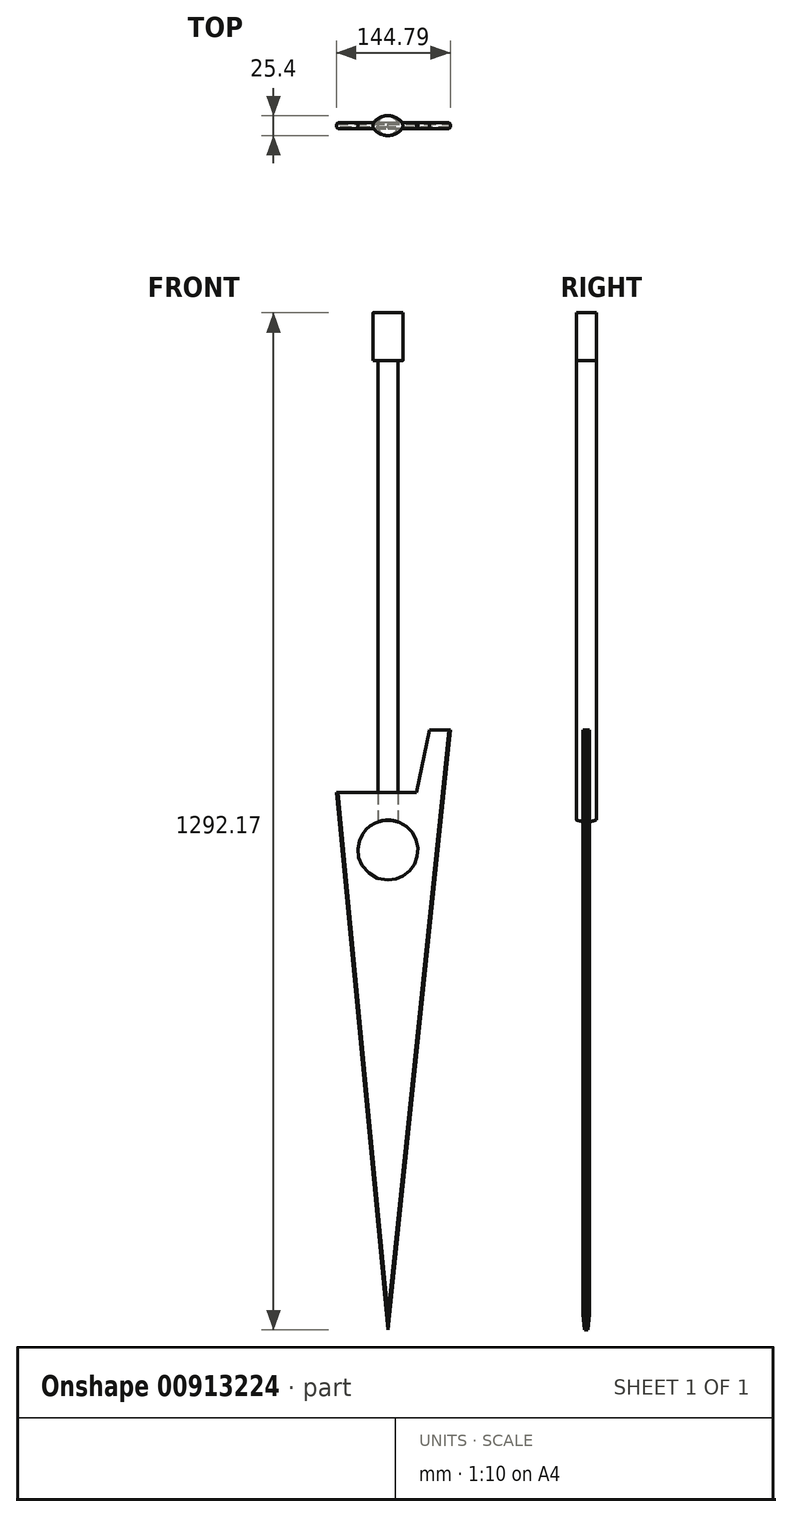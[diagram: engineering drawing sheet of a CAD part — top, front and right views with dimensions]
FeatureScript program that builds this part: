
annotation { "Feature Type Name" : "Feature", "Feature Type Description" : "" }
export const myFeature = defineFeature(function(context is Context, id is Id, definition is map)
    precondition{}
    {
        {
            var Q0;
            Q0=qCreatedBy(makeId("Front.planeOp"),FACE);
            var sketch = newSketch(context, id + "F0", { "sketchPlane" : qUnion([Q0])});
            skLineSegment(sketch, "E0", {"start": v(0, 0) * mm, "end": v(0, 609.6) * mm, "construction": true});
            skLineSegment(sketch, "E1", {"start": v(0, 0) * mm, "end": v(0, -609.6) * mm, "construction": true});
            skLineSegment(sketch, "E2", {"start": v(28.58, 0) * mm, "end": v(28.58, 304.8) * mm, "construction": true});
            skLineSegment(sketch, "E3", {"start": v(79.37, 152.4) * mm, "end": v(0, -609.6) * mm});
            skLineSegment(sketch, "E4", {"start": v(28.58, 152.4) * mm, "end": v(-73.03, 152.4) * mm, "construction": true});
            skLineSegment(sketch, "E5", {"start": v(-65.41, 72.97) * mm, "end": v(0, -609.6) * mm});
            skCircle(sketch, "E6", {"center": v(0, 0) * mm, "radius": 38.1 * mm});
            skPoint(sketch, "E7.orphan", {"position": v(-38.1, 0) * mm});
            skLineSegment(sketch, "E8", {"start": v(28.58, 152.4) * mm, "end": v(23.49, 72.97) * mm});
            skLineSegment(sketch, "E9", {"start": v(23.49, 72.97) * mm, "end": v(-65.41, 72.97) * mm});
            skLineSegment(sketch, "E10", {"start": v(28.58, 152.4) * mm, "end": v(79.38, 152.4) * mm});
            skPoint(sketch, "E11.orphan", {"position": v(95.36, 305.86) * mm});
            skLineSegment(sketch, "E12", {"start": v(-38.1, 0) * mm, "end": v(-58.42, 0) * mm, "construction": true});
            skLineSegment(sketch, "E13", {"start": v(38.1, 0) * mm, "end": v(63.5, 0) * mm, "construction": true});
            skSolve(sketch);
        }
        {
            var Q0;
            Q0=makeQuery(id+"F0.imprint","IMPRINT",FACE,{"disambiguationData":[TD([[makeQuery(id+"F0.imprint","IMPRINT",EDGE,{"derivedFrom":sQuery(id+"F0.wireOp",EDGE,"E3")}),-1.0]])]});
            extrude(context, id + "F1", {"entities" : qUnion([Q0]), "endBound" : BoundingType.SYMMETRIC, "depth" : 7.94 * mm, "offsetDistance" : 30.48 * mm});
        }
        {
            var Q0;
            Q0=makeQuery(id+"F1.opExtrude","SWEPT_FACE",FACE,{"disambiguationData":[OSD([sQuery(id+"F0.wireOp",EDGE,"E9")])]});
            var sketch = newSketch(context, id + "F2", { "sketchPlane" : qUnion([Q0])});
            skCircle(sketch, "E14", {"center": v(0, 0) * mm, "radius": 12.7 * mm});
            skSolve(sketch);
        }
        {
            var Q0;
            Q0 = qSketchRegion(id + "F2", true);
            var Q1;
            Q1=makeQuery(id+"F1.opExtrude","SWEPT_FACE",FACE,{"disambiguationData":[OSD([sQuery(id+"F0.wireOp",EDGE,"E6")])]});
            extrude(context, id + "F3", {"entities" : qUnion([Q0]), "depth" : 609.6 * mm, "offsetDistance" : 30.48 * mm, "hasSecondDirection" : true, "secondDirectionBound" : SecondDirectionBoundingType.UP_TO_SURFACE, "secondDirectionOppositeDirection" : true, "secondDirectionDepth" : 25.4 * mm, "secondDirectionBoundEntityFace" : qUnion([Q1])});
        }
        {
            var Q0;
            {var subQ0=sQuery(id+"F2.wireOp",EDGE,"E14");var subQ1=sQuery(id+"F0.wireOp",EDGE,"E9");var subQ2=makeQuery(id+"F1.opExtrude","CAP_EDGE",EDGE,{"disambiguationData":[OSD([subQ1])],"isStart":true});var subQ3=makeQuery(id+"F2.imprint","INTERSECT",VERTEX,{"disambiguationData":[OD(0.0)],"derivedFrom":[subQ2,subQ0]});Q0=makeQuery(id+"F3.opExtrude","CAP_FACE",FACE,{"disambiguationData":[OSD([subQ0]),topologyDisambiguationEdgeConnected([makeQuery(id+"F2.imprint","IMPRINT",EDGE,{"disambiguationData":[TD([[subQ3,1.0]])],"derivedFrom":subQ0})])],"isStart":false});}
            var sketch = newSketch(context, id + "F4", { "sketchPlane" : qUnion([Q0])});
            skLineSegment(sketch, "E15.bottom", {"start": v(22.86, 12.7) * mm, "end": v(-22.86, 12.7) * mm});
            skLineSegment(sketch, "E15.top", {"start": v(22.86, -12.7) * mm, "end": v(-22.86, -12.7) * mm});
            skLineSegment(sketch, "E15.left", {"start": v(22.86, 12.7) * mm, "end": v(22.86, -12.7) * mm});
            skLineSegment(sketch, "E15.right", {"start": v(-22.86, 12.7) * mm, "end": v(-22.86, -12.7) * mm});
            skPoint(sketch, "E15.middle", {"position": v(0, 0) * mm});
            skSolve(sketch);
        }
        {
            var Q0;
            Q0 = qSketchRegion(id + "F4", true);
            extrude(context, id + "F5", {"entities" : qUnion([Q0]), "operationType" : NewBodyOperationType.ADD, "oppositeDirection" : true, "depth" : 60.96 * mm, "offsetDistance" : 30.48 * mm});
        }
        {
            var Q0;
            Q0=makeQuery(id+"F5.opExtrude","SWEPT_EDGE",EDGE,{"disambiguationData":[OSD([sQuery(id+"F4.wireOp",EDGE,"E15.top"),sQuery(id+"F4.wireOp",EDGE,"E15.left")])]});
            var Q1;
            Q1=makeQuery(id+"F5.opExtrude","SWEPT_EDGE",EDGE,{"disambiguationData":[OSD([sQuery(id+"F4.wireOp",EDGE,"E15.top"),sQuery(id+"F4.wireOp",EDGE,"E15.right")])]});
            var Q2;
            Q2=makeQuery(id+"F5.opExtrude","SWEPT_EDGE",EDGE,{"disambiguationData":[OSD([sQuery(id+"F4.wireOp",EDGE,"E15.bottom"),sQuery(id+"F4.wireOp",EDGE,"E15.right")])]});
            var Q3;
            Q3=makeQuery(id+"F5.opExtrude","SWEPT_EDGE",EDGE,{"disambiguationData":[OSD([sQuery(id+"F4.wireOp",EDGE,"E15.bottom"),sQuery(id+"F4.wireOp",EDGE,"E15.left")])]});
            fillet(context, id + "F6", {"entities" : qUnion([Q0, Q1, Q2, Q3]), "radius" : 22.86 * mm, "tangentPropagation" : true, "allowEdgeOverflow" : false});
        }
        {
            var Q0;
            Q0=makeQuery(id+"F1.opExtrude","CAP_EDGE",EDGE,{"disambiguationData":[OSD([sQuery(id+"F0.wireOp",EDGE,"E3")])],"isStart":false});
            var Q1;
            Q1=makeQuery(id+"F1.opExtrude","CAP_EDGE",EDGE,{"disambiguationData":[OSD([sQuery(id+"F0.wireOp",EDGE,"E3")])],"isStart":true});
            chamfer(context, id + "F7", {"entities" : qUnion([Q0, Q1]), "width" : 1.9 * mm, "tangentPropagation" : true});
        }
        {
            var Q0;
            {var subQ0=sQuery(id+"F4.wireOp",EDGE,"E15.right");Q0=makeQuery(id+"F6.opFillet","BLEND_EDGE",EDGE,{"blendedFrom":[makeQuery(id+"F5.opExtrude","SWEPT_EDGE",EDGE,{"disambiguationData":[OSD([sQuery(id+"F4.wireOp",EDGE,"E15.bottom"),subQ0])]}),makeQuery(id+"F5.opExtrude","SWEPT_EDGE",EDGE,{"disambiguationData":[OSD([sQuery(id+"F4.wireOp",EDGE,"E15.top"),subQ0])]})],"blendedInto":[]});}
            var Q1;
            {var subQ0=sQuery(id+"F4.wireOp",EDGE,"E15.left");Q1=makeQuery(id+"F6.opFillet","BLEND_EDGE",EDGE,{"blendedFrom":[makeQuery(id+"F5.opExtrude","SWEPT_EDGE",EDGE,{"disambiguationData":[OSD([sQuery(id+"F4.wireOp",EDGE,"E15.bottom"),subQ0])]}),makeQuery(id+"F5.opExtrude","SWEPT_EDGE",EDGE,{"disambiguationData":[OSD([sQuery(id+"F4.wireOp",EDGE,"E15.top"),subQ0])]})],"blendedInto":[]});}
            fillet(context, id + "F8", {"entities" : qUnion([Q0, Q1]), "radius" : 7.62 * mm, "tangentPropagation" : true, "allowEdgeOverflow" : false});
        }
        {
            var Q0;
            Q0=makeQuery(id+"F1.opExtrude","CAP_EDGE",EDGE,{"disambiguationData":[OSD([sQuery(id+"F0.wireOp",EDGE,"E6")])],"isStart":true});
            var Q1;
            Q1=makeQuery(id+"F1.opExtrude","CAP_EDGE",EDGE,{"disambiguationData":[OSD([sQuery(id+"F0.wireOp",EDGE,"E6")])],"isStart":false});
            fillet(context, id + "F9", {"entities" : qUnion([Q0, Q1]), "radius" : 3.97 * mm, "tangentPropagation" : true, "defaultsChanged" : true, "vertexSettings" : [], "allowEdgeOverflow" : false});
        }
        {
            var Q0;
            Q0=makeQuery(id+"F1.opExtrude","CAP_EDGE",EDGE,{"disambiguationData":[OSD([sQuery(id+"F0.wireOp",EDGE,"E5")])],"isStart":true});
            var Q1;
            Q1=makeQuery(id+"F1.opExtrude","CAP_EDGE",EDGE,{"disambiguationData":[OSD([sQuery(id+"F0.wireOp",EDGE,"E5")])],"isStart":false});
            chamfer(context, id + "F10", {"entities" : qUnion([Q0, Q1]), "width" : 1.9 * mm, "tangentPropagation" : true});
        }
        {
            var Q0;
            Q0=makeQuery(id+"F1.opExtrude","CAP_FACE",FACE,{"disambiguationData":[OSD([sQuery(id+"F0.wireOp",EDGE,"E3"),sQuery(id+"F0.wireOp",EDGE,"E5"),sQuery(id+"F0.wireOp",EDGE,"E6"),sQuery(id+"F0.wireOp",EDGE,"E8"),sQuery(id+"F0.wireOp",EDGE,"E9"),sQuery(id+"F0.wireOp",EDGE,"E10")])],"isStart":false});
            var sketch = newSketch(context, id + "F11", { "sketchPlane" : qUnion([Q0])});
            skLineSegment(sketch, "E16", {"start": v(28.58, 152.4) * mm, "end": v(53.02, 152.4) * mm});
            skLineSegment(sketch, "E17", {"start": v(28.58, 152.4) * mm, "end": v(23.49, 72.97) * mm});
            skLineSegment(sketch, "E18", {"start": v(23.49, 72.97) * mm, "end": v(36.19, 72.97) * mm});
            skLineSegment(sketch, "E19", {"start": v(53.02, 152.4) * mm, "end": v(36.19, 72.97) * mm});
            skSolve(sketch);
        }
        {
            var Q0;
            Q0 = qSketchRegion(id + "F11", true);
            extrude(context, id + "F12", {"entities" : qUnion([Q0]), "operationType" : NewBodyOperationType.REMOVE, "oppositeDirection" : true, "depth" : 25.4 * mm, "offsetDistance" : 25.4 * mm});
        }
    });
